# Revit family: Drain-Cornice-6_Inch_Diameter-Zurn-Z181
name_source: partatom
category: Plumbing Fixtures
units: mm (PartAtom-declared; Revit-internal decimal feet)

## family parameters
Always vertical = Yes
Cut with Voids When Loaded = No
Maintain Annotation Orientation = No
OmniClass Number = 23.70.50.21.24.14
OmniClass Title = Deck Waste Water Drains
Part Type = Normal
Room Calculation Point = No
Round Connector Dimension = Use Radius
Shared = No
Work Plane-Based = No

## types (8) — shared parameters
Assembly Code = D2030300
CW Connection = No
Default Elevation = 3 "
Description = 6 [152] DIAMETER CORNICE DRAIN BOTTOM OUTLET
Dome Open Area (Sq. In) = 11 "
HW Connection = No
Main Material = Iron - Zurn - Cast - Painted - Blue
Manufacturer = Zurn Water, LCC
Manufacurer Brand = Zurn
Model = Z181
Modified Date = 08/22/2025
Product Documentation Link = https://files.zurn.com
Product Installation Sheet URL = https://files.zurn.com
Product Page URL = https://www.zurn.com
Product data url = https://www.bimobject.com
URL = www.zurn.com
Vent Connection = No
WFU = 1
Waste Connection = Yes
zero-valued in all types: CWFU, HWFU

## per-type parameters (varying)
| type | Approx. Weight (Lbs) | Body HT. Dimension - E | Body Outer Diameter | Connector Radius | Dome Material | Outlet Diamter A (Inner) | Outlet Diamter A (Nominal) | Outlet Diamter A (Outer) | Type Comments |
| ZRB181-3IP | 6 " | 2 " | 4.313 " | 1.5 " | Bronze - Zurn - Plain | 3.068 " | 3 " | 3.5 " | ZRB181-3 Inch Threaded Outlet with Cornice Drain |
| ZRB181-4IP | 7 " | 2 " | 5.25 " | 2 " | Bronze - Zurn - Plain | 4.026 " | 4 " | 4.5 " | ZRB181-4 Inch Threaded Outlet with Cornice Drain |
| ZRB181-3NH | 6 " | 4.5 " | 4.313 " | 1.5 " | Bronze - Zurn - Plain | 3.068 " | 3 " | 3.5 " | ZRB181-3 Inch No-Hub Outlet with Cornice Drain |
| ZRB181-4NH | 7 " | 4.5 " | 5.25 " | 2 " | Bronze - Zurn - Plain | 4.026 " | 4 " | 4.5 " | ZRB181-4 Inch No-Hub Outlet with Cornice Drain |
| ZN181-3IP | 6 " | 2 " | 4.313 " | 1.5 " | Bronze - Zurn - Polished Nickel | 3.068 " | 3 " | 3.5 " | ZN181-3 Inch Threaded Outlet with Cornice Drain |
| ZN181-4IP | 7 " | 2 " | 5.25 " | 2 " | Bronze - Zurn - Polished Nickel | 4.026 " | 4 " | 4.5 " | ZN181-4 Inch Threaded Outlet with Cornice Drain |
| ZN181-3NH | 6 " | 4.5 " | 4.313 " | 1.5 " | Bronze - Zurn - Polished Nickel | 3.068 " | 3 " | 3.5 " | ZN181-3 Inch No-Hub Outlet with Cornice Drain |
| ZN181-4NH | 7 " | 4.5 " | 5.25 " | 2 " | Bronze - Zurn - Polished Nickel | 4.026 " | 4 " | 4.5 " | ZN181-4 Inch No-Hub Outlet with Cornice Drain |

## geometry (parser evidence)
native form markers: Sweep x2
no freeform markers — native parametric forms only
